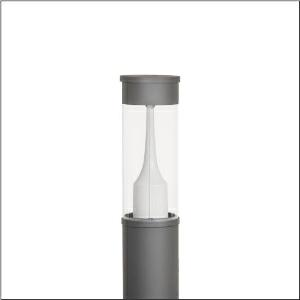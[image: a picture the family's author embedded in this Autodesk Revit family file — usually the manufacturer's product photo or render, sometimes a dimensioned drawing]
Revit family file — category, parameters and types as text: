
# Revit family: city-light_120_iq___pl1_2s_5xa5285rf14h_2286
name_source: partatom
category: Lighting Fixtures
units: mm (PartAtom-declared; Revit-internal decimal feet)

## family parameters
Cut with Voids When Loaded = No
Host = Face
Light Source = No
Part Type = Normal
Room Calculation Point = No
Round Connector Dimension = Use Diameter
Shared = No

## types (1)
- --- (1 x LED, 2970 lm, 18.5 W, 4000K)
    Apparent Load = 19 VA
    CIE Flux Codes = 23 62 94 96 100
    Color Rendering = 70
    Color Temperature = 4000K
    Default Elevation = 1800 mm
    Description = City-Light 120 iQ, bollard luminaire, Module 540 iQ-SR, primary light control with 3 zone facetted reflector, of plastic, silver coated, highly specular, structured, primary optical cover: cover, of PMMA, transparent, partly coated, light distribution: PL1.2s, primary light characteristic: symmetric, LED, High Power LED, rated luminous flux: 2.970lm, luminous efficacy: 161lm/W, light colour: 740, colour temperature: 4000K, control gear: ECG iQ, control: pre-setting: logarithmic dimming characteristic, Street-Remote, Auto-Match, Temp-Guard, Lumen-Switch, Night-Set, Smart-Wire, Light-Fading, Desk-Remote (wireless, voltage-free reading and setting of iQ features in the workshop via application-optimized NFC function/RFID function), optimised constant luminous flux control (CLO 2.0), with terminal, 6-pole, max. 2.5mm², mains connection: 230..240V, AC, 50/60Hz, start of lifetime: 19W, end of service life: 20W, reduction: 9W, luminaire housing, cylindrical, of extruded aluminium section, coated, Siteco® metallic grey (DB 702S), length: 1.200mm, diameter: 200mm, Module 540 iQ-SR, traffic white (RAL 9016), equipment: standard, protection rating (complete): IP54, insulation class (complete): insulation class II (safety insulation), certification: CE, ENEC, VDE, packaging unit: 1 piece

Light Distribution: PL1.2s
    Height = 500 mm
    Lamp = 1 x LED
    Lamp Light Flux = 2970 lm
    Lamp Power = 18.5 W
    Lamp count = 1
    Length = 200 mm  [stored 0.656168 ft]
    Luminous efficacy = 161 lm/W
    Manufacturer = Siteco
    ModVariant = No
    Model = 5XA5285RF14H
    Mounting Place = Floor
    Mounting Type = Freestanding
    Number of Poles = 1
    OnlyDefault = Yes
    Power Factor = 1
    Product Name = City-Light 120 iQ | PL1.2s
    Product group = bollard luminaire
    ProductGroupID = 1304
    Protection Class = Protection class II
    Protection Degree = IP 54
    RLX_Detail_Level = 1
    RLX_Emergency_Light_Flux = 0 lm
    RLX_Emergency_Type = 0
    RLX_Emergency_Type_DB = No
    RlxData = <blob elided: 30313 chars, md5=f7af3eb5>
    Socket = socket
    Standby Power = 0 W
    System Light Flux = 2970 lm
    System Power = 19 W
    Type Comments = factory setting: luminous flux: 100 % | dim-lin: 254 | 385 mA
    Type Image = l_1006922.jpg
    URL = http://relux.com
    VarID = @adj_115087
    Voltage = 0 V
    Weight = 0.00 kg
    Width = 0 mm  [stored 0 ft]

note: [stored X ft] marks values corroborated as IEEE doubles in the binary element streams (Revit-internal decimal feet)

## geometry (parser evidence)
native form markers: Blend x4, Sweep x10
no freeform markers — native parametric forms only
